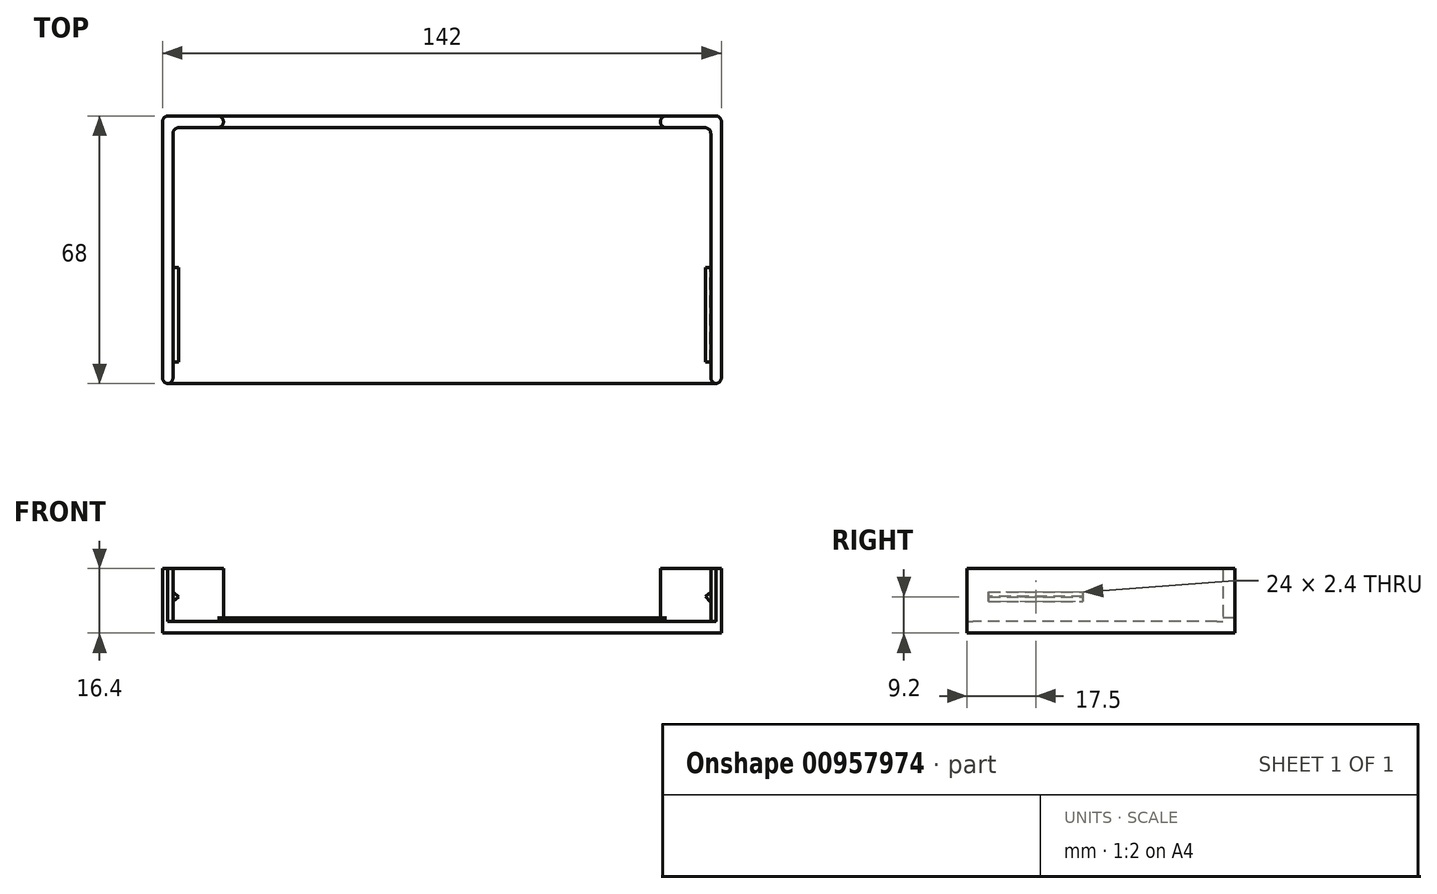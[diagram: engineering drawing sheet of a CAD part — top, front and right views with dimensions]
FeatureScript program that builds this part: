
annotation { "Feature Type Name" : "Feature", "Feature Type Description" : "" }
export const myFeature = defineFeature(function(context is Context, id is Id, definition is map)
    precondition{}
    {
        {
            var Q0;
            Q0=qCreatedBy(makeId("Top.planeOp"),FACE);
            var sketch = newSketch(context, id + "F0", { "sketchPlane" : qUnion([Q0])});
            skPoint(sketch, "E0.middle", {"position": v(0, 0) * mm});
            skLineSegment(sketch, "E1.bottom", {"start": v(71, -32.5) * mm, "end": v(-71, -32.5) * mm});
            skLineSegment(sketch, "E1.top", {"start": v(71, 32.5) * mm, "end": v(-71, 32.5) * mm});
            skLineSegment(sketch, "E1.left", {"start": v(71, -32.5) * mm, "end": v(71, 32.5) * mm});
            skLineSegment(sketch, "E1.right", {"start": v(-71, -32.5) * mm, "end": v(-71, 32.5) * mm});
            skLineSegment(sketch, "E2.bottom", {"start": v(-71, 32.5) * mm, "end": v(-68.3, 32.5) * mm});
            skLineSegment(sketch, "E2.top", {"start": v(-71, -32.5) * mm, "end": v(-68.3, -32.5) * mm});
            skLineSegment(sketch, "E2.left", {"start": v(-71, 32.5) * mm, "end": v(-71, -32.5) * mm});
            skLineSegment(sketch, "E2.right", {"start": v(-68.3, 32.5) * mm, "end": v(-68.3, -32.5) * mm});
            skLineSegment(sketch, "E3.bottom", {"start": v(71, 32.5) * mm, "end": v(68.3, 32.5) * mm});
            skLineSegment(sketch, "E3.top", {"start": v(71, -32.5) * mm, "end": v(68.3, -32.5) * mm});
            skLineSegment(sketch, "E3.left", {"start": v(71, 32.5) * mm, "end": v(71, -32.5) * mm});
            skLineSegment(sketch, "E3.right", {"start": v(68.3, 32.5) * mm, "end": v(68.3, -32.5) * mm});
            skLineSegment(sketch, "E4.bottom", {"start": v(-71, 32.5) * mm, "end": v(-55.5, 32.5) * mm});
            skLineSegment(sketch, "E4.top", {"start": v(-71, 35.5) * mm, "end": v(-55.5, 35.5) * mm});
            skLineSegment(sketch, "E4.left", {"start": v(-71, 32.5) * mm, "end": v(-71, 35.5) * mm});
            skLineSegment(sketch, "E4.right", {"start": v(-55.5, 32.5) * mm, "end": v(-55.5, 35.5) * mm});
            skLineSegment(sketch, "E5.bottom", {"start": v(71, 32.5) * mm, "end": v(55.5, 32.5) * mm});
            skLineSegment(sketch, "E5.top", {"start": v(71, 35.5) * mm, "end": v(55.5, 35.5) * mm});
            skLineSegment(sketch, "E5.left", {"start": v(71, 32.5) * mm, "end": v(71, 35.5) * mm});
            skLineSegment(sketch, "E5.right", {"start": v(55.5, 32.5) * mm, "end": v(55.5, 35.5) * mm});
            skLineSegment(sketch, "E6.bottom", {"start": v(55.5, 32.5) * mm, "end": v(-55.5, 32.5) * mm});
            skLineSegment(sketch, "E6.top", {"start": v(55.5, 35.5) * mm, "end": v(-55.5, 35.5) * mm});
            skSolve(sketch);
        }
        {
            var Q0;
            {var subQ0=sQuery(id+"F0.wireOp",EDGE,"E2.right");Q0=makeQuery(id+"F0.imprint","IMPRINT",FACE,{"disambiguationData":[TD([[makeQuery(id+"F0.imprint","IMPRINT",EDGE,{"derivedFrom":subQ0}),1.0]])]});}
            extrude(context, id + "F1", {"entities" : qUnion([Q0]), "depth" : 3 * mm, "offsetDistance" : 25 * mm});
        }
        {
            var Q0;
            Q0=makeQuery(id+"F0.imprint","IMPRINT",FACE,{"disambiguationData":[TD([[makeQuery(id+"F0.imprint","IMPRINT",EDGE,{"derivedFrom":sQuery(id+"F0.wireOp",EDGE,"E4.top")}),-1.0]])]});
            var Q1;
            {var subQ0=sQuery(id+"F0.wireOp",EDGE,"E1.right");Q1=makeQuery(id+"F0.imprint","IMPRINT",FACE,{"disambiguationData":[TD([[makeQuery(id+"F0.imprint","IMPRINT",EDGE,{"derivedFrom":subQ0}),-1.0]])]});}
            var Q2;
            Q2=makeQuery(id+"F0.imprint","IMPRINT",FACE,{"disambiguationData":[TD([[makeQuery(id+"F0.imprint","IMPRINT",EDGE,{"derivedFrom":sQuery(id+"F0.wireOp",EDGE,"E5.top")}),1.0]])]});
            var Q3;
            {var subQ2=sQuery(id+"F0.wireOp",EDGE,"E1.left");Q3=makeQuery(id+"F0.imprint","IMPRINT",FACE,{"disambiguationData":[TD([[makeQuery(id+"F0.imprint","IMPRINT",EDGE,{"derivedFrom":subQ2}),1.0]])]});}
            extrude(context, id + "F2", {"entities" : qUnion([Q0, Q1, Q2, Q3]), "operationType" : NewBodyOperationType.ADD, "depth" : 16.4 * mm, "offsetDistance" : 25 * mm});
        }
        {
            var Q0;
            {var subQ2=sQuery(id+"F0.wireOp",EDGE,"E4.right");Q0=makeQuery(id+"F0.imprint","IMPRINT",FACE,{"disambiguationData":[TD([[makeQuery(id+"F0.imprint","IMPRINT",EDGE,{"derivedFrom":subQ2}),-1.0]])]});}
            extrude(context, id + "F3", {"entities" : qUnion([Q0]), "operationType" : NewBodyOperationType.ADD, "depth" : 3.8 * mm, "offsetDistance" : 25 * mm});
        }
        {
            var Q0;
            Q0=makeQuery(id+"F2.opExtrude","SWEPT_FACE",FACE,{"disambiguationData":[OSD([sQuery(id+"F0.wireOp",EDGE,"E2.right")])]});
            var sketch = newSketch(context, id + "F4", { "sketchPlane" : qUnion([Q0])});
            skLineSegment(sketch, "E7.bottom", {"start": v(-27, 10.4) * mm, "end": v(-3, 10.4) * mm});
            skLineSegment(sketch, "E7.top", {"start": v(-27, 8) * mm, "end": v(-3, 8) * mm});
            skLineSegment(sketch, "E7.left", {"start": v(-27, 10.4) * mm, "end": v(-27, 8) * mm});
            skLineSegment(sketch, "E7.right", {"start": v(-3, 10.4) * mm, "end": v(-3, 8) * mm});
            skSolve(sketch);
        }
        {
            var Q0;
            Q0=makeQuery(id+"F4.imprint","IMPRINT",FACE,{"disambiguationData":[TD([[makeQuery(id+"F4.imprint","IMPRINT",EDGE,{"derivedFrom":sQuery(id+"F4.wireOp",EDGE,"E7.bottom")}),-1.0]])]});
            extrude(context, id + "F5", {"entities" : qUnion([Q0]), "operationType" : NewBodyOperationType.ADD, "depth" : 1.5 * mm, "offsetDistance" : 25 * mm});
        }
        {
            var Q0;
            Q0=makeQuery(id+"F2.opExtrude","SWEPT_FACE",FACE,{"disambiguationData":[OSD([sQuery(id+"F0.wireOp",EDGE,"E3.right")])]});
            var sketch = newSketch(context, id + "F6", { "sketchPlane" : qUnion([Q0])});
            skLineSegment(sketch, "E8.bottom", {"start": v(3, 10.4) * mm, "end": v(27, 10.4) * mm});
            skLineSegment(sketch, "E8.top", {"start": v(3, 8) * mm, "end": v(27, 8) * mm});
            skLineSegment(sketch, "E8.left", {"start": v(3, 10.4) * mm, "end": v(3, 8) * mm});
            skLineSegment(sketch, "E8.right", {"start": v(27, 10.4) * mm, "end": v(27, 8) * mm});
            skSolve(sketch);
        }
        {
            var Q0;
            Q0=makeQuery(id+"F6.imprint","IMPRINT",FACE,{"disambiguationData":[TD([[makeQuery(id+"F6.imprint","IMPRINT",EDGE,{"derivedFrom":sQuery(id+"F6.wireOp",EDGE,"E8.bottom")}),-1.0]])]});
            extrude(context, id + "F7", {"entities" : qUnion([Q0]), "operationType" : NewBodyOperationType.ADD, "depth" : 1.5 * mm, "offsetDistance" : 25 * mm});
        }
        {
            var Q0;
            Q0=makeQuery(id+"F5.opExtrude","CAP_EDGE",EDGE,{"disambiguationData":[OSD([sQuery(id+"F4.wireOp",EDGE,"E7.bottom")])],"isStart":false});
            var Q1;
            Q1=makeQuery(id+"F7.opExtrude","CAP_EDGE",EDGE,{"disambiguationData":[OSD([sQuery(id+"F6.wireOp",EDGE,"E8.bottom")])],"isStart":false});
            var Q2;
            Q2=makeQuery(id+"F5.opExtrude","CAP_EDGE",EDGE,{"disambiguationData":[OSD([sQuery(id+"F4.wireOp",EDGE,"E7.top")])],"isStart":false});
            var Q3;
            Q3=makeQuery(id+"F7.opExtrude","CAP_EDGE",EDGE,{"disambiguationData":[OSD([sQuery(id+"F6.wireOp",EDGE,"E8.top")])],"isStart":false});
            chamfer(context, id + "F8", {"entities" : qUnion([Q0, Q1, Q2, Q3]), "chamferType" : ChamferType.OFFSET_ANGLE, "width" : 1.5 * mm, "oppositeDirection" : false, "angle" : 40 * degree, "tangentPropagation" : true});
        }
        {
            var Q0;
            Q0=makeQuery(id+"F2.opExtrude","SWEPT_EDGE",EDGE,{"disambiguationData":[OSD([sQuery(id+"F0.wireOp",EDGE,"E4.top"),sQuery(id+"F0.wireOp",EDGE,"E4.left")])]});
            var Q1;
            Q1=makeQuery(id+"F2.opExtrude","SWEPT_EDGE",EDGE,{"disambiguationData":[OSD([sQuery(id+"F0.wireOp",EDGE,"E1.bottom"),sQuery(id+"F0.wireOp",EDGE,"E1.right")])]});
            var Q2;
            Q2=makeQuery(id+"F2.opExtrude","SWEPT_EDGE",EDGE,{"disambiguationData":[OSD([sQuery(id+"F0.wireOp",EDGE,"E1.bottom"),sQuery(id+"F0.wireOp",EDGE,"E1.left")])]});
            var Q3;
            Q3=makeQuery(id+"F2.opExtrude","SWEPT_EDGE",EDGE,{"disambiguationData":[OSD([sQuery(id+"F0.wireOp",EDGE,"E5.top"),sQuery(id+"F0.wireOp",EDGE,"E5.left")])]});
            var Q4;
            Q4=makeQuery(id+"F2.opExtrude","SWEPT_EDGE",EDGE,{"disambiguationData":[OSD([sQuery(id+"F0.wireOp",EDGE,"E5.top"),sQuery(id+"F0.wireOp",EDGE,"E5.right"),sQuery(id+"F0.wireOp",EDGE,"E6.top")])]});
            var Q5;
            Q5=makeQuery(id+"F2.opExtrude","SWEPT_EDGE",EDGE,{"disambiguationData":[OSD([sQuery(id+"F0.wireOp",EDGE,"E4.top"),sQuery(id+"F0.wireOp",EDGE,"E4.right"),sQuery(id+"F0.wireOp",EDGE,"E6.top")])]});
            var Q6;
            {var subQ0=sQuery(id+"F0.wireOp",EDGE,"E1.top");var subQ1=sQuery(id+"F0.wireOp",EDGE,"E4.right");Q6=makeQuery(id+"F2.boolean.opBoolean","SPLIT",EDGE,{"disambiguationData":[topologyDisambiguationEdgeConnected([makeQuery(id+"F2.opExtrude","SWEPT_FACE",FACE,{"disambiguationData":[OSD([subQ0]),TDD([makeQuery(id+"F0.imprint","IMPRINT",EDGE,{"disambiguationData":[TD([[makeQuery(id+"F0.imprint","INTERSECT",VERTEX,{"derivedFrom":[subQ0,sQuery(id+"F0.wireOp",EDGE,"E2.right")]}),1.0]])],"derivedFrom":subQ0})])]})])],"derivedFrom":makeQuery(id+"F2.opExtrude","SWEPT_EDGE",EDGE,{"disambiguationData":[OSD([subQ0,subQ1])]})});}
            var Q7;
            Q7=makeQuery(id+"F2.opExtrude","SWEPT_EDGE",EDGE,{"disambiguationData":[OSD([sQuery(id+"F0.wireOp",EDGE,"E1.top"),sQuery(id+"F0.wireOp",EDGE,"E2.right")])]});
            var Q8;
            Q8=makeQuery(id+"F2.opExtrude","SWEPT_EDGE",EDGE,{"disambiguationData":[OSD([sQuery(id+"F0.wireOp",EDGE,"E1.bottom"),sQuery(id+"F0.wireOp",EDGE,"E2.right")])]});
            var Q9;
            {var subQ0=sQuery(id+"F0.wireOp",EDGE,"E5.right");var subQ1=sQuery(id+"F0.wireOp",EDGE,"E1.top");Q9=makeQuery(id+"F2.boolean.opBoolean","SPLIT",EDGE,{"disambiguationData":[topologyDisambiguationEdgeConnected([makeQuery(id+"F2.opExtrude","SWEPT_FACE",FACE,{"disambiguationData":[OSD([subQ1]),TDD([makeQuery(id+"F0.imprint","IMPRINT",EDGE,{"disambiguationData":[TD([[makeQuery(id+"F0.imprint","INTERSECT",VERTEX,{"derivedFrom":[subQ1,subQ0]}),1.0]])],"derivedFrom":subQ1})])]})])],"derivedFrom":makeQuery(id+"F2.opExtrude","SWEPT_EDGE",EDGE,{"disambiguationData":[OSD([subQ1,subQ0])]})});}
            var Q10;
            Q10=makeQuery(id+"F2.opExtrude","SWEPT_EDGE",EDGE,{"disambiguationData":[OSD([sQuery(id+"F0.wireOp",EDGE,"E1.top"),sQuery(id+"F0.wireOp",EDGE,"E3.right")])]});
            var Q11;
            Q11=makeQuery(id+"F2.opExtrude","SWEPT_EDGE",EDGE,{"disambiguationData":[OSD([sQuery(id+"F0.wireOp",EDGE,"E1.bottom"),sQuery(id+"F0.wireOp",EDGE,"E3.right")])]});
            fillet(context, id + "F9", {"entities" : qUnion([Q0, Q1, Q2, Q3, Q4, Q5, Q6, Q7, Q8, Q9, Q10, Q11]), "radius" : 1.5 * mm, "tangentPropagation" : true, "allowEdgeOverflow" : false});
        }
    });
